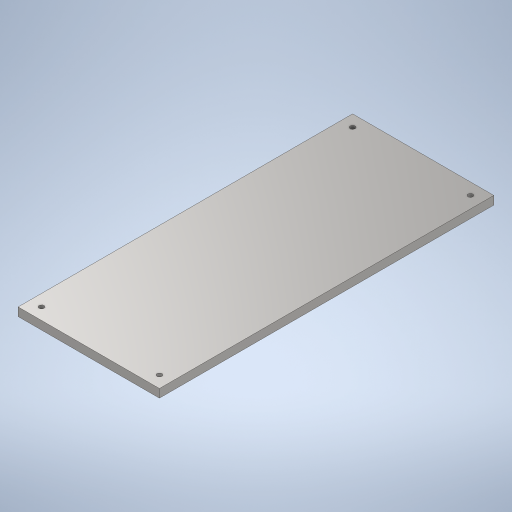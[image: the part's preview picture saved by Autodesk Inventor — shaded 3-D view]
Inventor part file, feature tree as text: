
AUTODESK INVENTOR PART (.ipt)
format: ipt  version: 2023.1 (Build 271208000, 208)  size: 249,344 bytes
history: native  units: in
note: dims shown in document units (in); Inventor stores cm internally (conversion verified against a paired STEP export)
features: extrude x2, sketch x2
ambient origin geometry x8: Origin, YZ Plane, XZ Plane, XY Plane, X Axis, Y Axis, Z Axis, Center Point
bodies: Solid1 (feature_tree)
feature tree (4):
  extrude  "Extrusion1"  Depth=0.1969in
  extrude  "Extrusion2"  Depth=0.1969in
  sketch  "Sketch1"  dims[d2=0.1969in d3=0.0in d4=0.1181in]
  sketch  "Sketch2"  dims[d5=0.1181in d6=0.1181in d7=0.1181in d8=0.2756in d9=0.2756in d10=0.2756in d11=0.2756in d12=0.2756in d13=0.2756in d14=0.2756in d15=0.2756in d16=0.1969in d17=0.0in]
